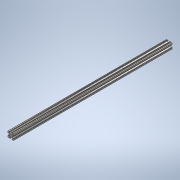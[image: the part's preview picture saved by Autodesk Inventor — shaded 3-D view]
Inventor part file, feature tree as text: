
AUTODESK INVENTOR PART (.ipt)
format: ipt  version: 2020 (Build 240168000, 168)  size: 243,200 bytes
history: native  units: in
note: dims shown in document units (in); Inventor stores cm internally (conversion verified against a paired STEP export)
features: extrude x1, sketch x1
ambient origin geometry x8: Origin, YZ Plane, XZ Plane, XY Plane, X Axis, Y Axis, Z Axis, Center Point
bodies: Solid1 (feature_tree)
feature tree (2):
  extrude  "Extrusion1"  [1 undecoded]
  sketch  "Sketch1"  dims[d0=26.0in d1=0.0in]
note: 1 required parameter value undecoded (feature->parameter linkage not recoverable at this tier; creation-order binding heuristic only, values carry confidence <= 0.55)
